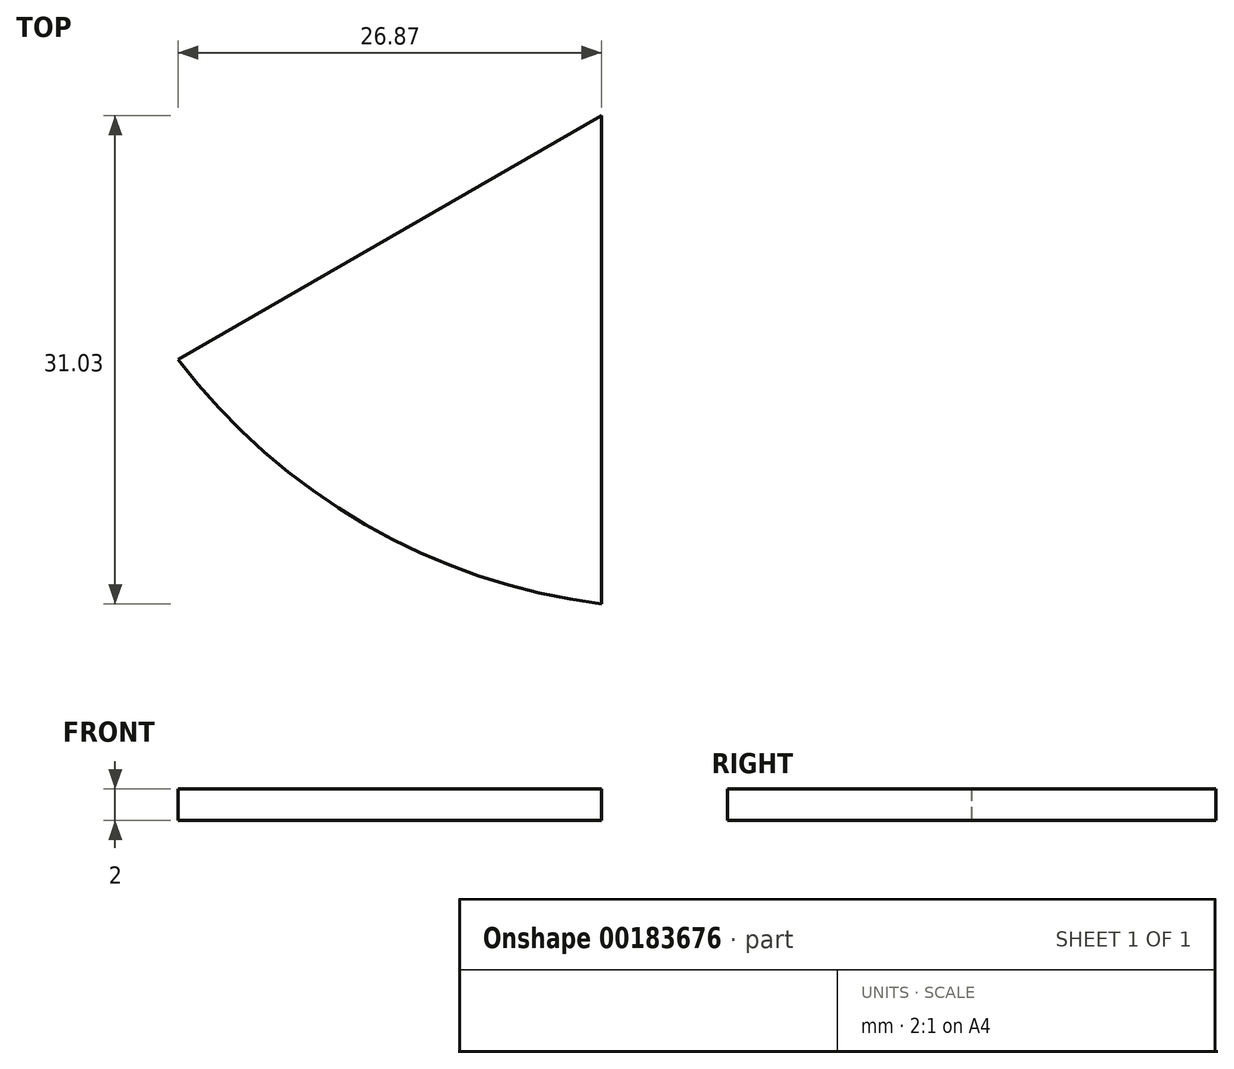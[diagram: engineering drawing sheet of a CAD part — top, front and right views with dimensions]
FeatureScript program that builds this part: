
annotation { "Feature Type Name" : "Feature", "Feature Type Description" : "" }
export const myFeature = defineFeature(function(context is Context, id is Id, definition is map)
    precondition{}
    {
        {
            var Q0;
            Q0=qCreatedBy(makeId("Top.planeOp"),FACE);
            var sketch = newSketch(context, id + "F0", { "sketchPlane" : qUnion([Q0])});
            skLineSegment(sketch, "E0", {"start": v(0, 0) * mm, "end": v(0, -31.03) * mm});
            skLineSegment(sketch, "E1", {"start": v(0, 0) * mm, "end": v(-26.87, -15.51) * mm});
            skArc(sketch, "E2", {"start": v(-26.87, -15.51) * mm, "mid": v(-15, -25.98) * mm, "end": v(0, -31.03) * mm});
            skLineSegment(sketch, "E3", {"start": v(-15, -25.98) * mm, "end": v(5, 8.66) * mm, "construction": true});
            skSolve(sketch);
        }
        {
            assignVariable(context, id + "F1", {"name" : "LayerDepth", "anyValue" : 2});
        }
        {
            var Q0;
            Q0 = qSketchRegion(id + "F0", true);
            extrude(context, id + "F2", {"entities" : qUnion([Q0]), "depth" : getVariable(context, 'LayerDepth') * mm});
        }
    });
